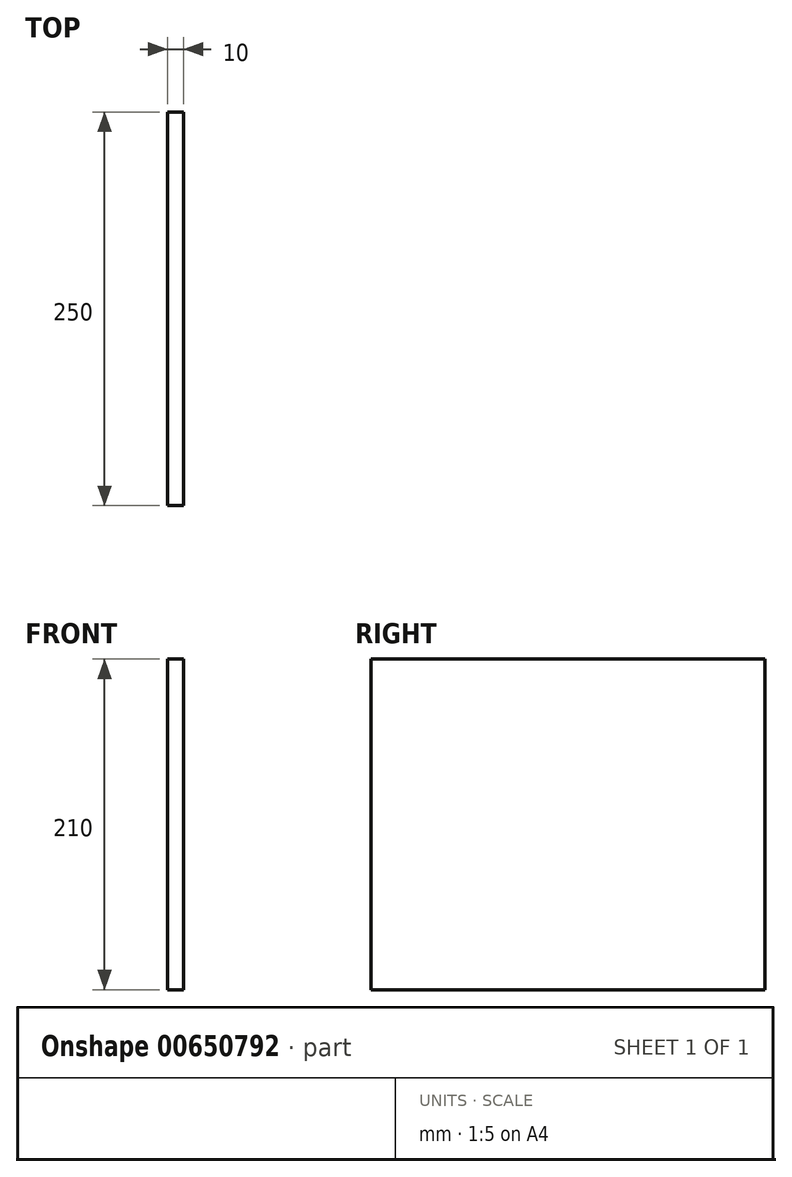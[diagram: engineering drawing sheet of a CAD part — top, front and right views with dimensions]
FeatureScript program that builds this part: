
annotation { "Feature Type Name" : "Feature", "Feature Type Description" : "" }
export const myFeature = defineFeature(function(context is Context, id is Id, definition is map)
    precondition{}
    {
        {
            var Q0;
            Q0=qCreatedBy(makeId("Right.planeOp"),FACE);
            var sketch = newSketch(context, id + "F0", { "sketchPlane" : qUnion([Q0])});
            skLineSegment(sketch, "E0.bottom", {"start": v(-92.1, 101.98) * mm, "end": v(157.9, 101.98) * mm});
            skLineSegment(sketch, "E0.top", {"start": v(-92.1, -108.02) * mm, "end": v(157.9, -108.02) * mm});
            skLineSegment(sketch, "E0.left", {"start": v(-92.1, 101.98) * mm, "end": v(-92.1, -108.02) * mm});
            skLineSegment(sketch, "E0.right", {"start": v(157.9, 101.98) * mm, "end": v(157.9, -108.02) * mm});
            skSolve(sketch);
        }
        {
            var Q0;
            Q0=qSketchRegion(id+"F0",true);
            extrude(context, id + "F1", {"entities" : qUnion([Q0]), "depth" : 10 * mm, "offsetDistance" : 25 * mm});
        }
    });
